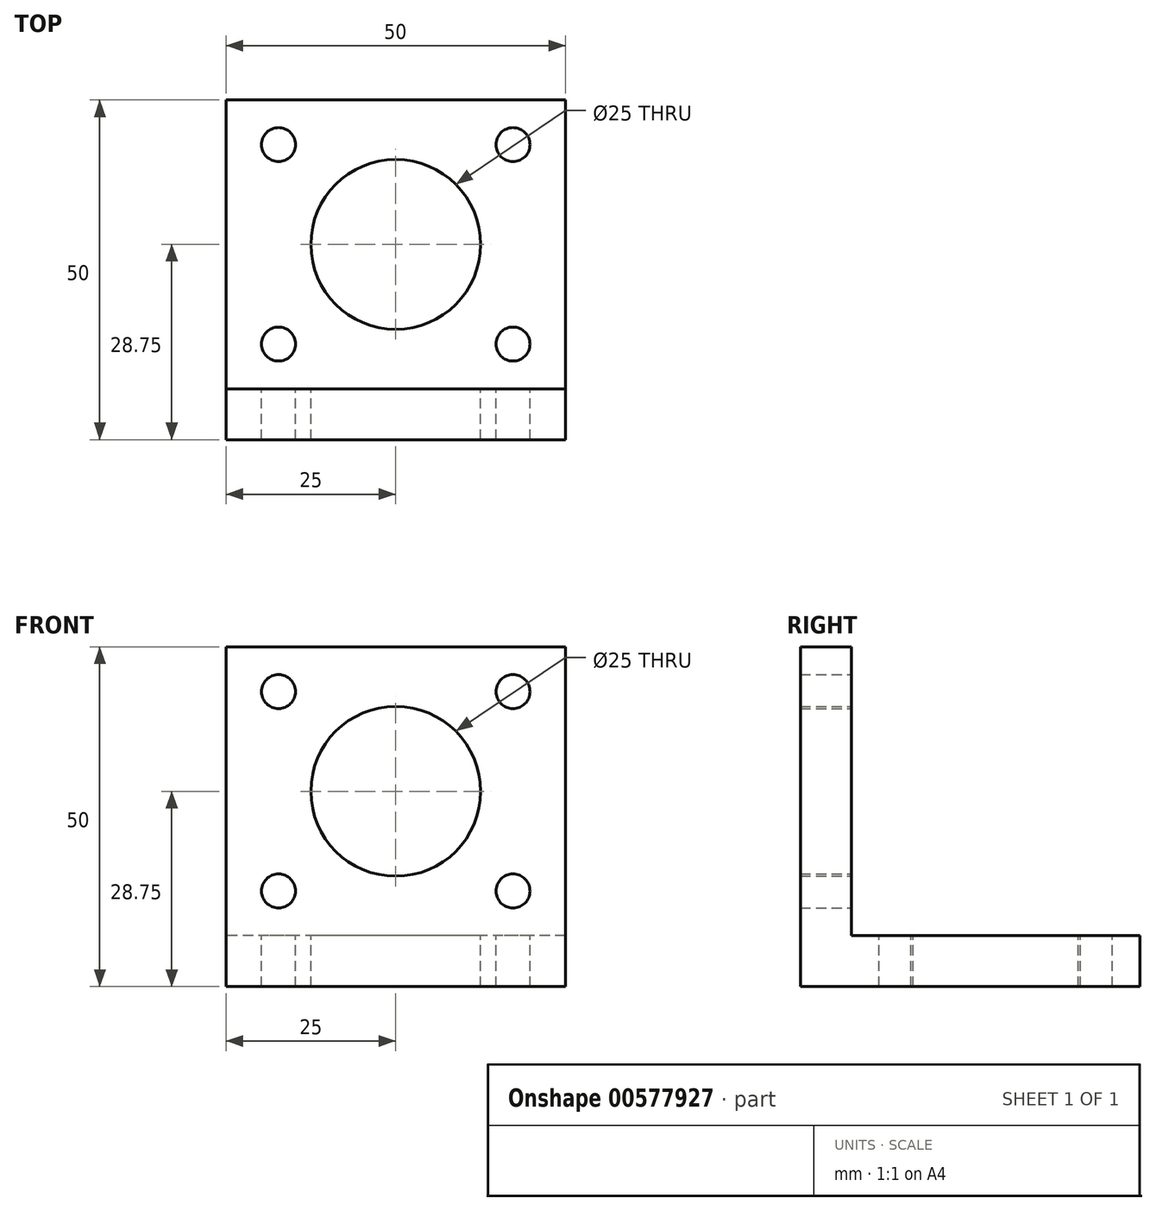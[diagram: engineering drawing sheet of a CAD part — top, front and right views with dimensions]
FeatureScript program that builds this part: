
annotation { "Feature Type Name" : "Feature", "Feature Type Description" : "" }
export const myFeature = defineFeature(function(context is Context, id is Id, definition is map)
    precondition{}
    {
        {
            var Q0;
            Q0=qCreatedBy(makeId("Right.planeOp"),FACE);
            var sketch = newSketch(context, id + "F0", { "sketchPlane" : qUnion([Q0])});
            skLineSegment(sketch, "E0", {"start": v(0, 50) * mm, "end": v(0, 0) * mm});
            skLineSegment(sketch, "E1", {"start": v(0, 0) * mm, "end": v(50, 0) * mm});
            skLineSegment(sketch, "E2", {"start": v(50, 0) * mm, "end": v(50, 7.5) * mm});
            skLineSegment(sketch, "E3", {"start": v(50, 7.5) * mm, "end": v(7.5, 7.5) * mm});
            skLineSegment(sketch, "E4", {"start": v(7.5, 7.5) * mm, "end": v(7.5, 50) * mm});
            skLineSegment(sketch, "E5", {"start": v(7.5, 50) * mm, "end": v(0, 50) * mm});
            skSolve(sketch);
        }
        {
            var Q0;
            Q0 = qSketchRegion(id + "F0", true);
            extrude(context, id + "F1", {"entities" : qUnion([Q0]), "depth" : 50 * mm, "offsetDistance" : 25 * mm});
        }
        {
            var Q0;
            Q0=makeQuery(id+"F1.opExtrude","SWEPT_FACE",FACE,{"disambiguationData":[OSD([sQuery(id+"F0.wireOp",EDGE,"E4")])]});
            var sketch = newSketch(context, id + "F2", { "sketchPlane" : qUnion([Q0])});
            skCircle(sketch, "E6", {"center": v(-25, 28.75) * mm, "radius": 12.5 * mm});
            skPoint(sketch, "E6.centerSnap0", {"position": v(-50, 28.75) * mm});
            skPoint(sketch, "E6.centerSnap1", {"position": v(-25, 50) * mm});
            skCircle(sketch, "E7", {"center": v(-42.26, 43.42) * mm, "radius": 2.5 * mm});
            skCircle(sketch, "E8", {"center": v(-7.74, 43.42) * mm, "radius": 2.5 * mm});
            skCircle(sketch, "E9", {"center": v(-7.74, 14.08) * mm, "radius": 2.5 * mm});
            skCircle(sketch, "E10", {"center": v(-42.26, 14.08) * mm, "radius": 2.5 * mm});
            skSolve(sketch);
        }
        {
            var Q0;
            Q0 = qSketchRegion(id + "F2", true);
            extrude(context, id + "F3", {"entities" : qUnion([Q0]), "operationType" : NewBodyOperationType.REMOVE, "endBound" : BoundingType.THROUGH_ALL, "oppositeDirection" : true, "depth" : 25 * mm, "offsetDistance" : 25 * mm});
        }
        {
            var Q0;
            Q0=makeQuery(id+"F1.opExtrude","SWEPT_FACE",FACE,{"disambiguationData":[OSD([sQuery(id+"F0.wireOp",EDGE,"E3")])]});
            var sketch = newSketch(context, id + "F4", { "sketchPlane" : qUnion([Q0])});
            skCircle(sketch, "E11", {"center": v(25, 28.75) * mm, "radius": 12.5 * mm});
            skPoint(sketch, "E11.centerSnap0", {"position": v(0, 28.75) * mm});
            skPoint(sketch, "E11.centerSnap1", {"position": v(25, 50) * mm});
            skCircle(sketch, "E12", {"center": v(7.74, 43.42) * mm, "radius": 2.5 * mm});
            skCircle(sketch, "E13", {"center": v(42.26, 43.42) * mm, "radius": 2.5 * mm});
            skCircle(sketch, "E14", {"center": v(42.26, 14.08) * mm, "radius": 2.5 * mm});
            skCircle(sketch, "E15", {"center": v(7.74, 14.08) * mm, "radius": 2.5 * mm});
            skSolve(sketch);
        }
        {
            var Q0;
            Q0 = qSketchRegion(id + "F4", true);
            extrude(context, id + "F5", {"entities" : qUnion([Q0]), "operationType" : NewBodyOperationType.REMOVE, "endBound" : BoundingType.THROUGH_ALL, "oppositeDirection" : true, "depth" : 25 * mm, "offsetDistance" : 25 * mm});
        }
    });
